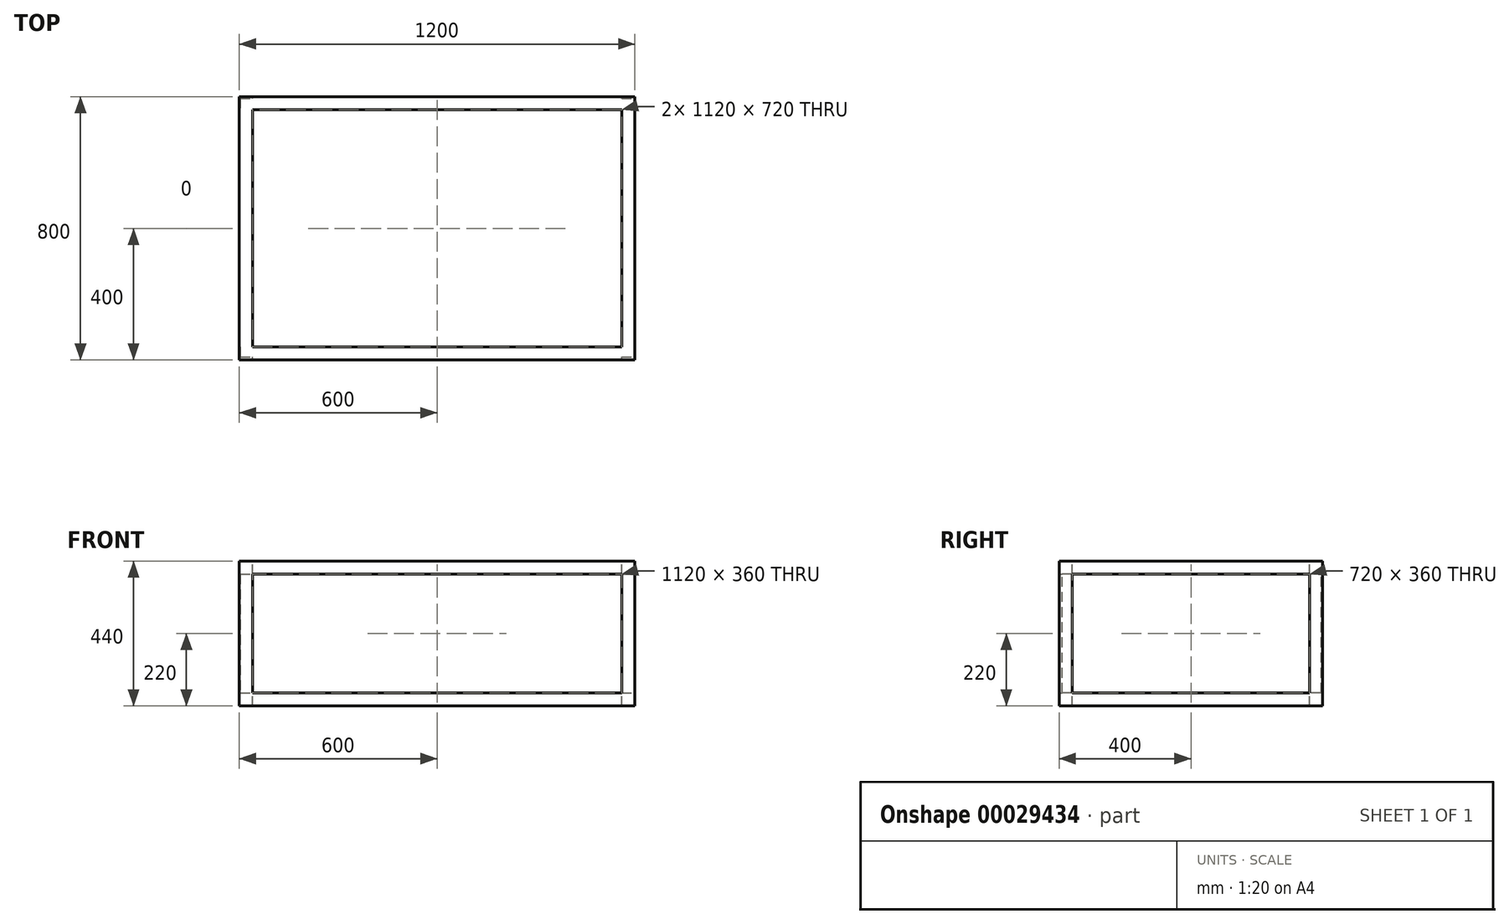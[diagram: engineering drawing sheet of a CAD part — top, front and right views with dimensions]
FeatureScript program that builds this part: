
annotation { "Feature Type Name" : "Feature", "Feature Type Description" : "" }
export const myFeature = defineFeature(function(context is Context, id is Id, definition is map)
    precondition{}
    {
        {
            var Q0;
            Q0=qCreatedBy(makeId("Top.planeOp"),FACE);
            var sketch = newSketch(context, id + "F0", { "sketchPlane" : qUnion([Q0])});
            skLineSegment(sketch, "E0.bottom", {"start": v(0, 0) * mm, "end": v(1200, 0) * mm});
            skLineSegment(sketch, "E0.top", {"start": v(0, -800) * mm, "end": v(1200, -800) * mm});
            skLineSegment(sketch, "E0.left", {"start": v(0, 0) * mm, "end": v(0, -800) * mm});
            skLineSegment(sketch, "E0.right", {"start": v(1200, 0) * mm, "end": v(1200, -800) * mm});
            skSolve(sketch);
        }
        {
            var Q0;
            Q0=makeQuery(id+"F0.imprint","IMPRINT",FACE,{"disambiguationData":[TD([[makeQuery(id+"F0.imprint","IMPRINT",EDGE,{"derivedFrom":sQuery(id+"F0.wireOp",EDGE,"E0.bottom")}),-1.0]])]});
            extrude(context, id + "F1", {"entities" : qUnion([Q0]), "depth" : 440 * mm});
        }
        {
            var Q0;
            Q0=makeQuery(id+"F1.opExtrude","CAP_FACE",FACE,{"disambiguationData":[OSD([sQuery(id+"F0.wireOp",EDGE,"E0.bottom"),sQuery(id+"F0.wireOp",EDGE,"E0.top"),sQuery(id+"F0.wireOp",EDGE,"E0.left"),sQuery(id+"F0.wireOp",EDGE,"E0.right")])],"isStart":false});
            var sketch = newSketch(context, id + "F2", { "sketchPlane" : qUnion([Q0])});
            skLineSegment(sketch, "E1.bottom", {"start": v(40, -40) * mm, "end": v(1160, -40) * mm});
            skLineSegment(sketch, "E1.top", {"start": v(40, -760) * mm, "end": v(1160, -760) * mm});
            skLineSegment(sketch, "E1.left", {"start": v(40, -40) * mm, "end": v(40, -760) * mm});
            skLineSegment(sketch, "E1.right", {"start": v(1160, -40) * mm, "end": v(1160, -760) * mm});
            skSolve(sketch);
        }
        {
            var Q0;
            Q0 = qSketchRegion(id + "F2", true);
            extrude(context, id + "F3", {"entities" : qUnion([Q0]), "operationType" : NewBodyOperationType.REMOVE, "oppositeDirection" : true, "depth" : 801.15 * mm});
        }
        {
            var Q0;
            Q0=makeQuery(id+"F1.opExtrude","SWEPT_FACE",FACE,{"disambiguationData":[OSD([sQuery(id+"F0.wireOp",EDGE,"E0.right")])]});
            var sketch = newSketch(context, id + "F4", { "sketchPlane" : qUnion([Q0])});
            skLineSegment(sketch, "E2.bottom", {"start": v(-760, 400) * mm, "end": v(-40, 400) * mm});
            skLineSegment(sketch, "E2.top", {"start": v(-760, 40) * mm, "end": v(-40, 40) * mm});
            skLineSegment(sketch, "E2.left", {"start": v(-760, 400) * mm, "end": v(-760, 40) * mm});
            skLineSegment(sketch, "E2.right", {"start": v(-40, 400) * mm, "end": v(-40, 40) * mm});
            skSolve(sketch);
        }
        {
            var Q0;
            Q0=makeQuery(id+"F4.imprint","IMPRINT",FACE,{"disambiguationData":[TD([[makeQuery(id+"F4.imprint","IMPRINT",EDGE,{"derivedFrom":sQuery(id+"F4.wireOp",EDGE,"E2.bottom")}),-1.0]])]});
            extrude(context, id + "F5", {"entities" : qUnion([Q0]), "operationType" : NewBodyOperationType.REMOVE, "oppositeDirection" : true, "depth" : 1490.35 * mm});
        }
        {
            var Q0;
            Q0=makeQuery(id+"F5.boolean.opBoolean","MERGE",FACE,{"derivedFrom":[makeQuery(id+"F3.boolean.opBoolean","COPY",FACE,{"derivedFrom":makeQuery(id+"F3.opExtrude","SWEPT_FACE",FACE,{"disambiguationData":[OSD([sQuery(id+"F2.wireOp",EDGE,"E1.bottom")])]})}),makeQuery(id+"F5.opExtrude","SWEPT_FACE",FACE,{"disambiguationData":[OSD([sQuery(id+"F4.wireOp",EDGE,"E2.right")])]})]});
            var sketch = newSketch(context, id + "F6", { "sketchPlane" : qUnion([Q0])});
            skLineSegment(sketch, "E3.bottom", {"start": v(3, 400) * mm, "end": v(1197, 400) * mm});
            skLineSegment(sketch, "E3.top", {"start": v(3, 40) * mm, "end": v(1197, 40) * mm});
            skLineSegment(sketch, "E3.left", {"start": v(3, 400) * mm, "end": v(3, 40) * mm});
            skLineSegment(sketch, "E3.right", {"start": v(1197, 400) * mm, "end": v(1197, 40) * mm});
            skSolve(sketch);
        }
        {
            var Q0;
            {var subQ1=sQuery(id+"F6.wireOp",EDGE,"E3.left");Q0=makeQuery(id+"F6.imprint","IMPRINT",FACE,{"disambiguationData":[TD([[makeQuery(id+"F6.imprint","IMPRINT",EDGE,{"derivedFrom":subQ1}),1.0]])]});}
            extrude(context, id + "F7", {"entities" : qUnion([Q0]), "operationType" : NewBodyOperationType.REMOVE, "oppositeDirection" : true, "depth" : 35 * mm, "hasSecondDirection" : true, "secondDirectionOppositeDirection" : false, "secondDirectionDepth" : 750 * mm});
        }
        {
            var Q0;
            Q0=makeQuery(id+"F1.opExtrude","SWEPT_FACE",FACE,{"disambiguationData":[OSD([sQuery(id+"F0.wireOp",EDGE,"E0.bottom")])]});
            var sketch = newSketch(context, id + "F8", { "sketchPlane" : qUnion([Q0])});
            skLineSegment(sketch, "E4.bottom", {"start": v(-1160, 400) * mm, "end": v(-40, 400) * mm});
            skLineSegment(sketch, "E4.top", {"start": v(-1160, 40) * mm, "end": v(-40, 40) * mm});
            skLineSegment(sketch, "E4.left", {"start": v(-1160, 400) * mm, "end": v(-1160, 40) * mm});
            skLineSegment(sketch, "E4.right", {"start": v(-40, 400) * mm, "end": v(-40, 40) * mm});
            skSolve(sketch);
        }
        {
            var Q0;
            Q0 = qSketchRegion(id + "F8", true);
            extrude(context, id + "F9", {"entities" : qUnion([Q0]), "operationType" : NewBodyOperationType.REMOVE, "oppositeDirection" : true, "depth" : 900 * mm});
        }
    });
